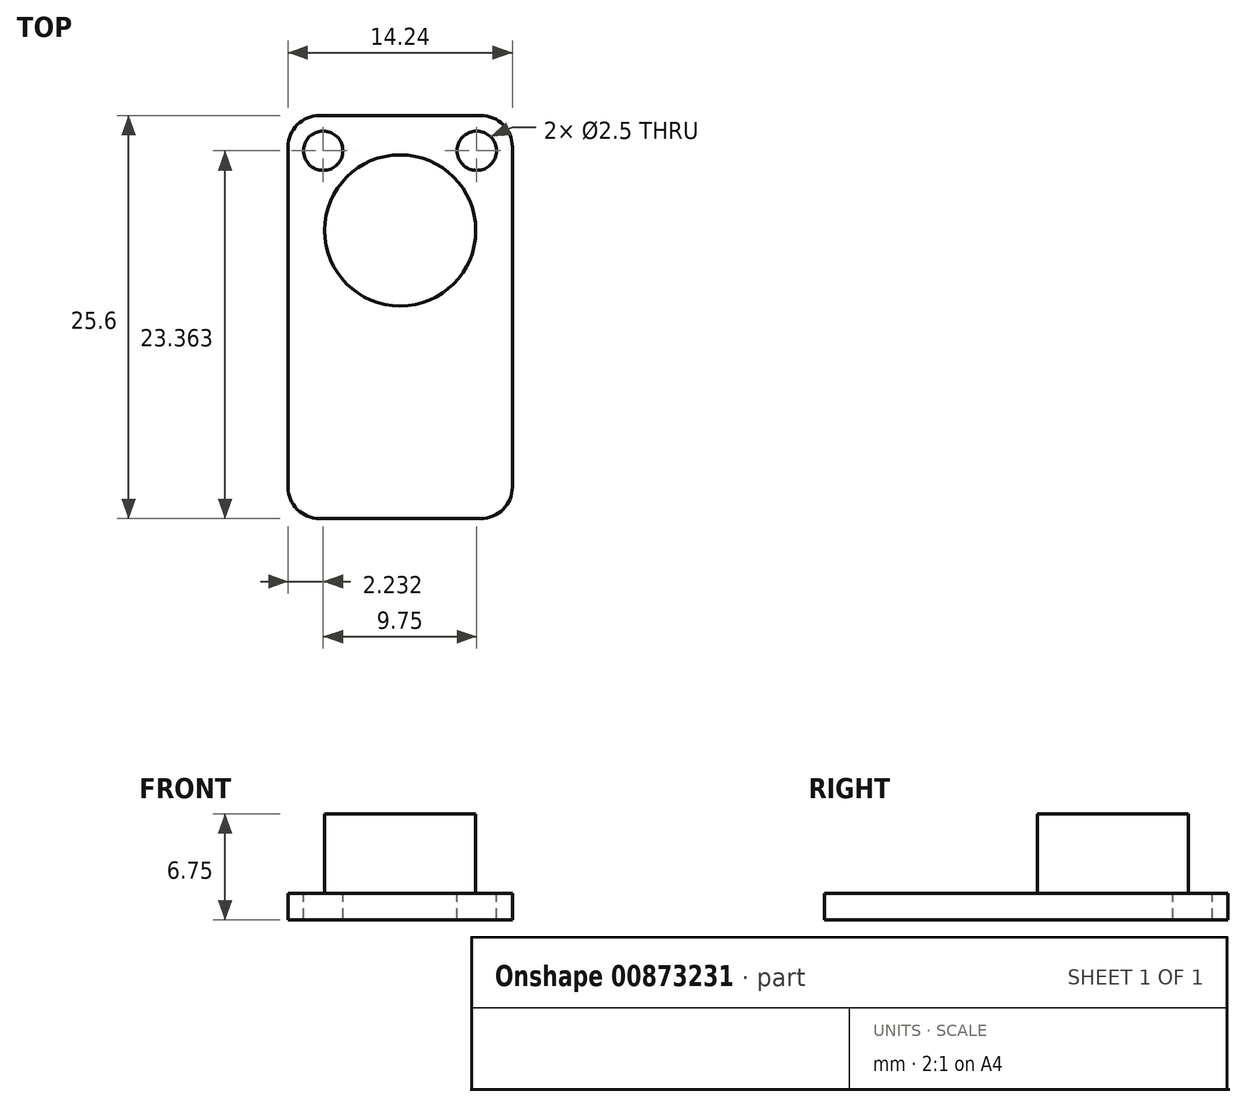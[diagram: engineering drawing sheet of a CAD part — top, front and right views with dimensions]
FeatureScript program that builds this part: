
annotation { "Feature Type Name" : "Feature", "Feature Type Description" : "" }
export const myFeature = defineFeature(function(context is Context, id is Id, definition is map)
    precondition{}
    {
        {
            assignVariable(context, id + "F0", {"name" : "board_thickness", "anyValue" : 1.7 * mm});
        }
        {
            assignVariable(context, id + "F1", {"name" : "mic_height", "anyValue" : 6.75 * mm - getVariable(context, 'board_thickness')});
        }
        {
            var Q0;
            Q0=qCreatedBy(makeId("Top.planeOp"),FACE);
            var sketch = newSketch(context, id + "F2", { "sketchPlane" : qUnion([Q0])});
            skLineSegment(sketch, "E0.bottom", {"start": v(-5.12, 12.8) * mm, "end": v(5.13, 12.8) * mm});
            skLineSegment(sketch, "E0.top", {"start": v(-5.13, -12.8) * mm, "end": v(5.12, -12.8) * mm});
            skLineSegment(sketch, "E0.left", {"start": v(-7.12, 10.8) * mm, "end": v(-7.13, -10.8) * mm});
            skLineSegment(sketch, "E0.right", {"start": v(7.13, 10.8) * mm, "end": v(7.12, -10.8) * mm});
            skLineSegment(sketch, "E1", {"start": v(-7.12, 12.8) * mm, "end": v(7.12, -12.8) * mm, "construction": true});
            skPoint(sketch, "E2", {"position": v(0, 0) * mm});
            skPoint(sketch, "E3.visualSharp", {"position": v(-7.12, 12.8) * mm});
            skArc(sketch, "E3.filletArc", {"start": v(-5.12, 12.8) * mm, "mid": v(-6.54, 12.21) * mm, "end": v(-7.12, 10.8) * mm});
            skPoint(sketch, "E4.visualSharp", {"position": v(7.13, 12.8) * mm});
            skArc(sketch, "E4.filletArc", {"start": v(7.13, 10.8) * mm, "mid": v(6.54, 12.21) * mm, "end": v(5.13, 12.8) * mm});
            skPoint(sketch, "E5.visualSharp", {"position": v(7.12, -12.8) * mm});
            skArc(sketch, "E5.filletArc", {"start": v(5.12, -12.8) * mm, "mid": v(6.54, -12.21) * mm, "end": v(7.12, -10.8) * mm});
            skPoint(sketch, "E6.visualSharp", {"position": v(-7.13, -12.8) * mm});
            skArc(sketch, "E6.filletArc", {"start": v(-7.13, -10.8) * mm, "mid": v(-6.54, -12.21) * mm, "end": v(-5.13, -12.8) * mm});
            skCircle(sketch, "E7", {"center": v(-4.89, 10.56) * mm, "radius": 1.25 * mm});
            skCircle(sketch, "E8.1.0.0", {"center": v(4.86, 10.56) * mm, "radius": 1.25 * mm});
            skLineSegment(sketch, "E8.direction1", {"start": v(-4.89, 10.56) * mm, "end": v(4.86, 10.56) * mm, "construction": true});
            skCircle(sketch, "E9", {"center": v(0, 5.5) * mm, "radius": 4.8 * mm});
            skSolve(sketch);
        }
        {
            var Q0;
            Q0=makeQuery(id+"F2.imprint","IMPRINT",FACE,{"disambiguationData":[TD([[makeQuery(id+"F2.imprint","IMPRINT",EDGE,{"derivedFrom":sQuery(id+"F2.wireOp",EDGE,"E9")}),1.0]])]});
            var Q1;
            Q1=makeQuery(id+"F2.imprint","IMPRINT",FACE,{"disambiguationData":[TD([[makeQuery(id+"F2.imprint","IMPRINT",EDGE,{"derivedFrom":sQuery(id+"F2.wireOp",EDGE,"E0.bottom")}),-1.0]])]});
            extrude(context, id + "F3", {"entities" : qUnion([Q0, Q1]), "oppositeDirection" : true, "depth" : getVariable(context, 'board_thickness'), "offsetDistance" : 25 * mm});
        }
        {
            var Q0;
            Q0=makeQuery(id+"F2.imprint","IMPRINT",FACE,{"disambiguationData":[TD([[makeQuery(id+"F2.imprint","IMPRINT",EDGE,{"derivedFrom":sQuery(id+"F2.wireOp",EDGE,"E9")}),1.0]])]});
            extrude(context, id + "F4", {"entities" : qUnion([Q0]), "operationType" : NewBodyOperationType.ADD, "depth" : getVariable(context, 'mic_height'), "offsetDistance" : 25 * mm});
        }
    });
